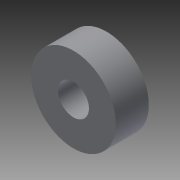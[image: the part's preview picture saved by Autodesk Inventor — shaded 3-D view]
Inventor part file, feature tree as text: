
AUTODESK INVENTOR PART (.ipt)
format: ipt  version: 2014 (Build 180170000, 170)  size: 83,968 bytes
history: native  units: in
note: dims shown in document units (in); Inventor stores cm internally (conversion verified against a paired STEP export)
features: plane x3, extrude x1, sketch x1
ambient origin geometry x8: Origin, YZ Plane, XZ Plane, XY Plane, X Axis, Y Axis, Z Axis, Center Point
bodies: Solid1 (feature_tree)
feature tree (5):
  extrude  "Extrusion1"  Depth=0.4in
  plane  "Work Plane1"
  plane  "Work Plane2"
  plane  "Work Plane3"
  sketch  "Sketch1"  dims[d0=1.025in d1=0.375in d2=0.4in d3=0.0in d4=0.0in d5=0.0in]
